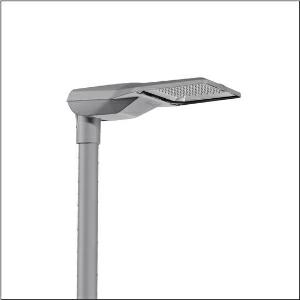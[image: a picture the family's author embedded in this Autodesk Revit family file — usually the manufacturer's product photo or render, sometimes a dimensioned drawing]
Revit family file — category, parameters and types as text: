
# Revit family: streetlight_sl_21_midi___st0_8a_5xe7c23a08nb_b441
name_source: partatom
category: Lighting Fixtures
units: mm (PartAtom-declared; Revit-internal decimal feet)

## family parameters
Cut with Voids When Loaded = No
Host = Face
Light Source = No
Part Type = Normal
Room Calculation Point = No
Round Connector Dimension = Use Diameter
Shared = No

## types (1)
- --- (1 x LED, 18780 lm, 151.2 W, 2200K)
    Apparent Load = 151 VA
    CIE Flux Codes = 41 75 97 100 100
    Color Rendering = 70
    Color Temperature = 2200K
    Default Elevation = 1800 mm
    Description = Streetlight SL 21 midi, mast luminaire, primary light control with lens, of PMMA, primary optical cover: cover, of toughened safety glass, transparent, light distribution: ST0.8a, light emission: direct distribution, primary light characteristic: asymmetric, installation type: post-top, side-entry, LED, 3G 1.5mm², High Power LED, rated luminous flux: 18.780lm, luminous efficacy: 124lm/W, light colour: 722, colour temperature: 2200K, control: overheat protection, constant luminous flux control, time-dependent luminous flux control, flexible luminous flux parameterisation, mains connection: 220..240V, AC, 50/60Hz, connection cable pre-assembled, cable length: 12,5m, wiring characteristics: H07RN-F, start of lifetime: 151W, end of service life: 157W, reduction: 70W, luminaire housing, of diecast aluminium, powder-coated, Siteco® metallic grey (DB 702S), corrosivity category C5 mid according to DIN EN ISO 12944, please order mast flange separately, inclination adjustable: 0°, 5°, 10°, 15°, sealing non-destructively replaceable, multi-level sealing system, length: 644mm, width: 335mm, height: 110mm, mast flange for spigot size: 42mm (side-entry): 5XC10008XM4, 60/48mm (side-entry/post-top): 5XC10108XM2, 76/60mm (side-entry/post-top): 5XC10108XM1, protection rating (complete): IP66, insulation class (complete): insulation class II (safety insulation), certification: CE, ENEC, ENEC+, VDE, impact resistance: IK09, permissible operating ambient temperature for outdoor applications: -40..+50°C, standard-compliant lighting for roads and squares, packaging unit: 1 piece

Light Distribution: ST0.8a
    Height = 111 mm
    Lamp = 1 x LED
    Lamp Light Flux = 18780 lm
    Lamp Power = 151.2 W
    Lamp count = 1
    Length = 644 mm
    Luminous efficacy = 124 lm/W
    Manufacturer = Siteco
    ModVariant = No
    Model = 5XE7C23A08NB
    Number of Poles = 1
    OnlyDefault = Yes
    Power Factor = 1
    Product Name = Streetlight SL 21 midi | ST0.8a
    Product group = mast luminaire | pylon top
    ProductGroupID = 6100
    Protection Class = Protection class II
    Protection Degree = IP 66
    RLX_Detail_Level = 1
    RLX_Emergency_Light_Flux = 0 lm
    RLX_Emergency_Type = 0
    RLX_Emergency_Type_DB = No
    RlxData = <blob elided: 90489 chars, md5=e991926f>
    Socket = socket
    Standby Power = 0 W
    System Light Flux = 18781 lm
    System Power = 151 W
    Type Comments = factory setting: luminous flux: 100 % | Output Level: 100 % | 802 mA
    Type Image = l_1004298.jpg
    URL = http://relux.com
    VarID = @adj_118811
    Voltage = 0 V
    Weight = 0.00 kg
    Width = 336 mm

## geometry (parser evidence)
native form markers: Blend x4, Sweep x10
no freeform markers — native parametric forms only
